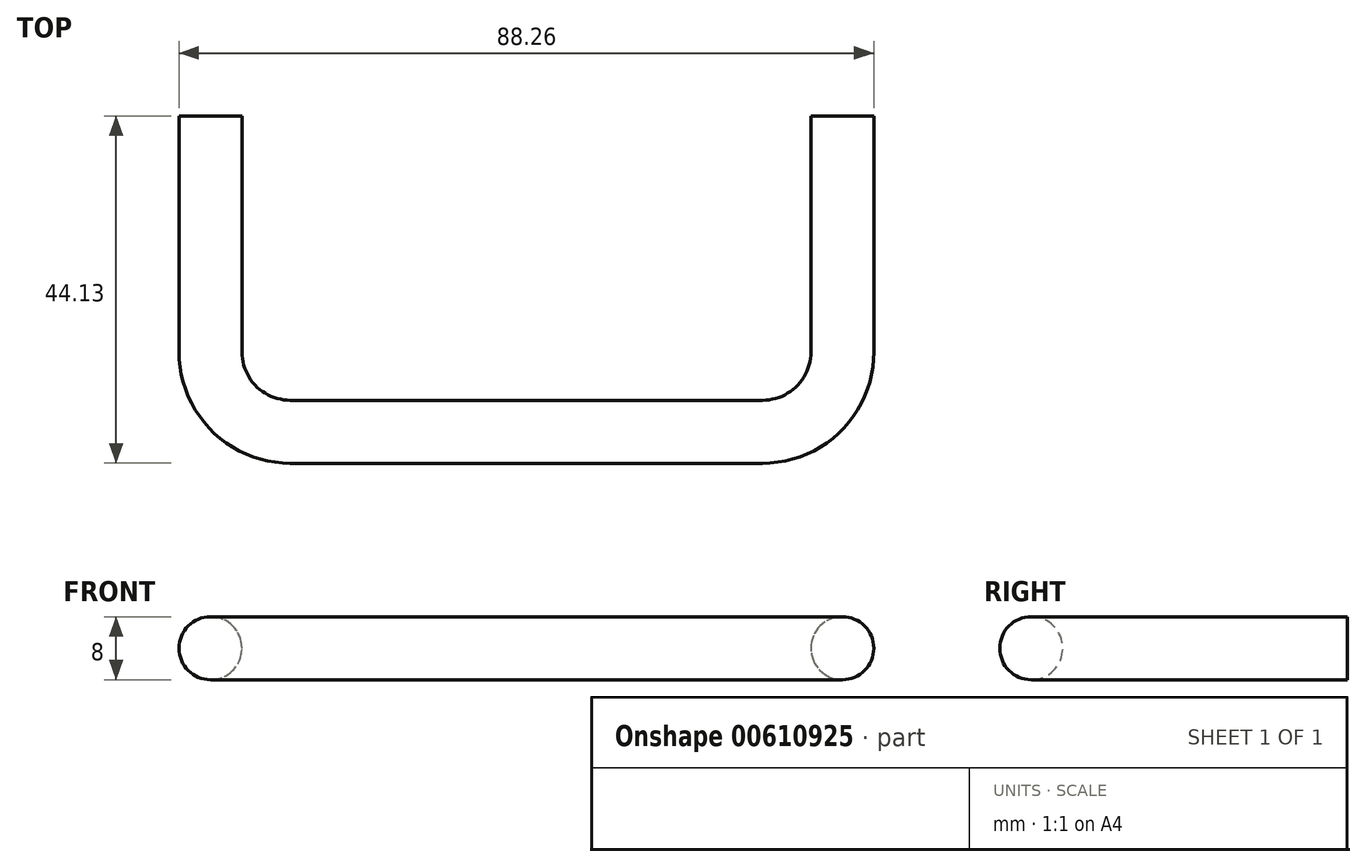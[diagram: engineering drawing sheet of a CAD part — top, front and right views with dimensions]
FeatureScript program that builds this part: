
annotation { "Feature Type Name" : "Feature", "Feature Type Description" : "" }
export const myFeature = defineFeature(function(context is Context, id is Id, definition is map)
    precondition{}
    {
        {
            var Q0;
            Q0=qCreatedBy(makeId("Top.planeOp"),FACE);
            var sketch = newSketch(context, id + "F0", { "sketchPlane" : qUnion([Q0])});
            skLineSegment(sketch, "E0", {"start": v(-40, 0) * mm, "end": v(-40, -30) * mm});
            skLineSegment(sketch, "E1", {"start": v(-30, -40) * mm, "end": v(0, -40) * mm});
            skLineSegment(sketch, "E2", {"start": v(40, -30) * mm, "end": v(40, 0) * mm});
            skPoint(sketch, "E3.visualSharp", {"position": v(-40, -40) * mm});
            skArc(sketch, "E3.filletArc", {"start": v(-40, -30) * mm, "mid": v(-37.07, -37.07) * mm, "end": v(-30, -40) * mm});
            skPoint(sketch, "E4.visualSharp", {"position": v(40, -40) * mm});
            skArc(sketch, "E4.filletArc", {"start": v(30, -40) * mm, "mid": v(37.07, -37.07) * mm, "end": v(40, -30) * mm});
            skLineSegment(sketch, "E5", {"start": v(0, -40) * mm, "end": v(30, -40) * mm});
            skSolve(sketch);
        }
        {
            var Q0;
            Q0=qCreatedBy(makeId("Front.planeOp"),FACE);
            var sketch = newSketch(context, id + "F1", { "sketchPlane" : qUnion([Q0])});
            skCircle(sketch, "E6", {"center": v(-40.13, 0) * mm, "radius": 4 * mm});
            skSolve(sketch);
        }
        {
            var Q0;
            Q0=makeQuery(id+"F1.imprint","IMPRINT",FACE,{"disambiguationData":[TD([[makeQuery(id+"F1.imprint","IMPRINT",EDGE,{"derivedFrom":sQuery(id+"F1.wireOp",EDGE,"E6")}),1.0]])]});
            var Q1;
            Q1=sQuery(id+"F0.wireOp",EDGE,"E0");
            var Q2;
            Q2=sQuery(id+"F0.wireOp",EDGE,"E3.filletArc");
            var Q3;
            Q3=sQuery(id+"F0.wireOp",EDGE,"E1");
            var Q4;
            Q4=sQuery(id+"F0.wireOp",EDGE,"E5");
            var Q5;
            Q5=sQuery(id+"F0.wireOp",EDGE,"E4.filletArc");
            var Q6;
            Q6=sQuery(id+"F0.wireOp",EDGE,"E2");
            sweep(context, id + "F2", {"profiles" : qUnion([Q0]), "path" : qUnion([Q1, Q2, Q3, Q4, Q5, Q6])});
        }
    });
